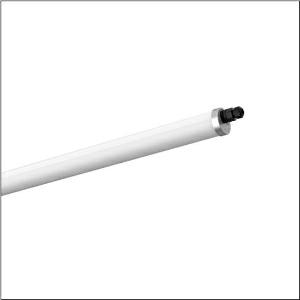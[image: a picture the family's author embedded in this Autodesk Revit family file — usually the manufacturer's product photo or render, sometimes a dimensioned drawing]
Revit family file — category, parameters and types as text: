
# Revit family: monsun_r__31_tube_51ft107n460a_2b58
name_source: partatom
category: Lighting Fixtures
units: mm (PartAtom-declared; Revit-internal decimal feet)

## family parameters
Cut with Voids When Loaded = No
Host = Face
Light Source = No
Part Type = Normal
Room Calculation Point = No
Round Connector Dimension = Use Diameter
Shared = No

## types (1)
- Monsun® 31 Tube (1 x LED, 6500 lm, 40 W, 4000K)
    Apparent Load = 40 VA
    CIE Flux Codes = 42 71 90 91 100
    Color Rendering = 80
    Color Temperature = 4000K
    Default Elevation = 1800 mm
    Description = Monsun® 31 Tube, tubular luminaire, primary optical cover: diffuser, of PMMA, light emission: direct distribution, primary light characteristic: symmetric, installation type: suspended mounting, surface-mounted, LED, rated luminous flux: 6.500lm, luminous efficacy: 160lm/W, light colour: 840, colour temperature: 4000K, control gear: ON/OFF, with with 1 terminal, 3-pole, max. 2.5mm², through-wiring: 3x 1.5mm², mains connection: 220..240V, AC, 50/60Hz, rated input power: 40W, housing, cylindrical, of PMMA, semi-transparent, matt white, with luminaire and ceiling fastening, V4A, mounting with brackets of stainless steel, length: 1.560mm, diameter: 75mm, end cap, of stainless steel (V4A), protection rating (complete): IP67/IP69K, insulation class (complete): insulation class I (protective earthing), certification: CE, UKCA, impact resistance: IK07, permissible operating ambient temperature: -20..+40°C, corresponds to IFS (International Featured Standards) requirements for safety and quality in the food industry, usage in unprotected outdoor areas possible with horizontal mounting, contact your sales advisor before using the luminaires in applications with unclear chemical exposure, large temperature fluctuations or condensation-forming humidity, packaging unit: 1 piece
    Height = 83 mm
    Lamp = 1 x LED
    Lamp Light Flux = 6500 lm
    Lamp Power = 40 W
    Lamp count = 1
    Length = 1560 mm
    Luminous efficacy = 163 lm/W
    Manufacturer = Siteco
    ModVariant = No
    Model = 51FT107N460A
    Mounting Place = Ceiling
    Mounting Type = Pendant
    Number of Poles = 1
    OnlyDefault = Yes
    Power Factor = 1
    Product Name = Monsun® 31 Tube
    Product group = tubular luminaire
    ProductGroupID = 906
    Protection Class = Protection class I
    RLX_Detail_Level = 1
    RLX_Emergency_Light_Flux = 0 lm
    RLX_Emergency_Type = 0
    RLX_Emergency_Type_DB = No
    RlxData = <blob elided: 25285 chars, md5=1d93332a>
    Socket = socket
    Standby Power = 0 W
    System Light Flux = 6500 lm
    System Power = 40 W
    Type Comments = Product without accessories
    Type Image = l_1228461.jpg
    URL = http://relux.com
    VarID = ---
    Voltage = 0 V
    Weight = 0.00 kg
    Width = 75 mm

## geometry (parser evidence)
native form markers: Blend x4, Sweep x13
no freeform markers — native parametric forms only
